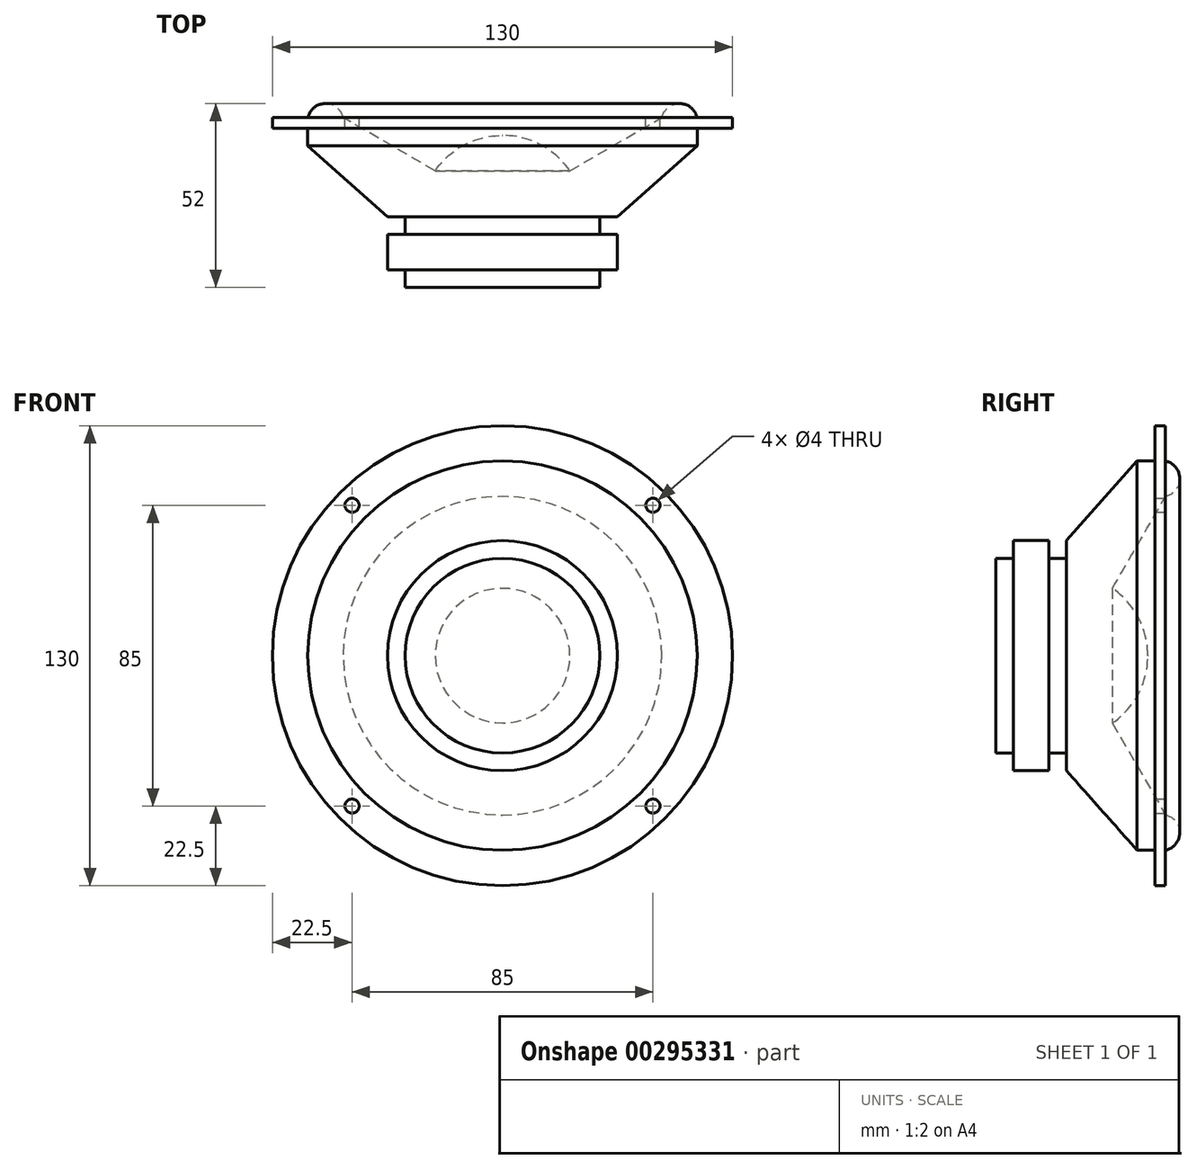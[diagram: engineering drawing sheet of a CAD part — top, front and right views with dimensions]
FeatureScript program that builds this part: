
annotation { "Feature Type Name" : "Feature", "Feature Type Description" : "" }
export const myFeature = defineFeature(function(context is Context, id is Id, definition is map)
    precondition{}
    {
        {
            var Q0;
            Q0=qCreatedBy(makeId("Front.planeOp"),FACE);
            var sketch = newSketch(context, id + "F0", { "sketchPlane" : qUnion([Q0])});
            skPoint(sketch, "E0.middle", {"position": v(0, 0) * mm});
            skCircle(sketch, "E1", {"center": v(0, 0) * mm, "radius": 55 * mm});
            skSolve(sketch);
        }
        {
            var Q0;
            Q0=makeQuery(id+"F0.imprint","IMPRINT",FACE,{"disambiguationData":[TD([[makeQuery(id+"F0.imprint","IMPRINT",EDGE,{"derivedFrom":sQuery(id+"F0.wireOp",EDGE,"E1")}),1.0]])]});
            extrude(context, id + "F1", {"entities" : qUnion([Q0]), "depth" : 25 * mm, "offsetDistance" : 25 * mm});
        }
        {
            var Q0;
            Q0=makeQuery(id+"F1.opExtrude","CAP_EDGE",EDGE,{"disambiguationData":[OSD([sQuery(id+"F0.wireOp",EDGE,"E1")])],"isStart":false});
            chamfer(context, id + "F2", {"entities" : qUnion([Q0]), "chamferType" : ChamferType.TWO_OFFSETS, "width1" : (45 / 2) * mm, "oppositeDirection" : false, "width2" : 20 * mm, "tangentPropagation" : true});
        }
        {
            var Q0;
            Q0=makeQuery(id+"F1.opExtrude","CAP_FACE",FACE,{"disambiguationData":[OSD([sQuery(id+"F0.wireOp",EDGE,"E1")])],"isStart":false});
            var sketch = newSketch(context, id + "F3", { "sketchPlane" : qUnion([Q0])});
            skCircle(sketch, "E2", {"center": v(0, 0) * mm, "radius": 27.5 * mm});
            skSolve(sketch);
        }
        {
            var Q0;
            Q0 = qSketchRegion(id + "F3", true);
            extrude(context, id + "F4", {"entities" : qUnion([Q0]), "depth" : 20 * mm, "offsetDistance" : 25 * mm});
        }
        {
            var Q0;
            Q0=makeQuery(id+"F4.opExtrude","CAP_FACE",FACE,{"disambiguationData":[OSD([sQuery(id+"F3.wireOp",EDGE,"E2")])],"isStart":false});
            var sketch = newSketch(context, id + "F5", { "sketchPlane" : qUnion([Q0])});
            skCircle(sketch, "E3", {"center": v(0, 0) * mm, "radius": 27.5 * mm});
            skCircle(sketch, "E4", {"center": v(0, 0) * mm, "radius": 32.5 * mm});
            skSolve(sketch);
        }
        {
            var Q0;
            Q0 = qSketchRegion(id + "F5", true);
            extrude(context, id + "F6", {"entities" : qUnion([Q0]), "operationType" : NewBodyOperationType.ADD, "endBound" : BoundingType.UP_TO_NEXT, "oppositeDirection" : true, "depth" : 10 * mm, "hasOffset" : true, "offsetDistance" : 5 * mm, "hasSecondDirection" : true, "secondDirectionOppositeDirection" : true, "secondDirectionDepth" : 5 * mm});
        }
        {
            var Q0;
            Q0=makeQuery(id+"F1.opExtrude","CAP_FACE",FACE,{"disambiguationData":[OSD([sQuery(id+"F0.wireOp",EDGE,"E1")])],"isStart":true});
            var sketch = newSketch(context, id + "F7", { "sketchPlane" : qUnion([Q0])});
            skCircle(sketch, "E5", {"center": v(0, 0) * mm, "radius": 65 * mm});
            skSolve(sketch);
        }
        {
            var Q0;
            Q0 = qSketchRegion(id + "F7", true);
            extrude(context, id + "F8", {"entities" : qUnion([Q0]), "operationType" : NewBodyOperationType.ADD, "depth" : 3 * mm, "offsetDistance" : 25 * mm});
        }
        {
            var Q0;
            Q0=makeQuery(id+"F8.opExtrude","CAP_FACE",FACE,{"disambiguationData":[OSD([sQuery(id+"F7.wireOp",EDGE,"E5")])],"isStart":false});
            var sketch = newSketch(context, id + "F9", { "sketchPlane" : qUnion([Q0])});
            skLineSegment(sketch, "E6.bottom", {"start": v(42.5, 42.5) * mm, "end": v(-42.5, 42.5) * mm, "construction": true});
            skLineSegment(sketch, "E6.top", {"start": v(42.5, -42.5) * mm, "end": v(-42.5, -42.5) * mm, "construction": true});
            skLineSegment(sketch, "E6.left", {"start": v(42.5, 42.5) * mm, "end": v(42.5, -42.5) * mm, "construction": true});
            skLineSegment(sketch, "E6.right", {"start": v(-42.5, 42.5) * mm, "end": v(-42.5, -42.5) * mm, "construction": true});
            skPoint(sketch, "E6.middle", {"position": v(0, 0) * mm});
            skCircle(sketch, "E7", {"center": v(-42.5, 42.5) * mm, "radius": 2 * mm});
            skCircle(sketch, "E8", {"center": v(42.5, 42.5) * mm, "radius": 2 * mm});
            skCircle(sketch, "E9", {"center": v(42.5, -42.5) * mm, "radius": 2 * mm});
            skCircle(sketch, "E10", {"center": v(-42.5, -42.5) * mm, "radius": 2 * mm});
            skSolve(sketch);
        }
        {
            var Q0;
            Q0 = qSketchRegion(id + "F9", true);
            extrude(context, id + "F10", {"entities" : qUnion([Q0]), "operationType" : NewBodyOperationType.REMOVE, "oppositeDirection" : true, "depth" : 25 * mm, "offsetDistance" : 25 * mm});
        }
        {
            var Q0;
            {var subQ0=sQuery(id+"F7.wireOp",EDGE,"E5");Q0=makeQuery(id+"FatyRIqTTuHNhlh_2.boolean.opBoolean","MERGE",FACE,{"derivedFrom":[makeQuery(id+"F8.opExtrude","CAP_FACE",FACE,{"disambiguationData":[OSD([subQ0])],"isStart":false}),makeQuery(id+"FatyRIqTTuHNhlh_2.opExtrude","CAP_FACE",FACE,{"disambiguationData":[OSD([subQ0,sQuery(id+"FaATDU1hy0XoADp_2.wireOp",EDGE,"dcB08ZIa-KRAl-nOKl-CVy3-LE7ijL8snLUQ")])],"isStart":true}),makeQuery(id+"FatyRIqTTuHNhlh_2.opExtrude","CAP_FACE",FACE,{"disambiguationData":[OSD([subQ0,sQuery(id+"FaATDU1hy0XoADp_2.wireOp",EDGE,"e9bd69b6-5c76-43c4-bfeb-50936e70dc3c.1.0")])],"isStart":true}),makeQuery(id+"FatyRIqTTuHNhlh_2.opExtrude","CAP_FACE",FACE,{"disambiguationData":[OSD([subQ0,sQuery(id+"FaATDU1hy0XoADp_2.wireOp",EDGE,"e9bd69b6-5c76-43c4-bfeb-50936e70dc3c.2.0")])],"isStart":true}),makeQuery(id+"FatyRIqTTuHNhlh_2.opExtrude","CAP_FACE",FACE,{"disambiguationData":[OSD([subQ0,sQuery(id+"FaATDU1hy0XoADp_2.wireOp",EDGE,"e9bd69b6-5c76-43c4-bfeb-50936e70dc3c.3.0")])],"isStart":true})]});}
            var sketch = newSketch(context, id + "F11", { "sketchPlane" : qUnion([Q0])});
            skCircle(sketch, "E11", {"center": v(0, 0) * mm, "radius": 45 * mm});
            skSolve(sketch);
        }
        {
            var Q0;
            Q0 = qSketchRegion(id + "F11", true);
            extrude(context, id + "F12", {"entities" : qUnion([Q0]), "operationType" : NewBodyOperationType.REMOVE, "oppositeDirection" : true, "depth" : 15 * mm, "offsetDistance" : 25 * mm, "hasDraft" : true, "draftAngle" : 60 * degree, "draftPullDirection" : true});
        }
        {
            var Q0;
            Q0=makeQuery(id+"F12.boolean.opBoolean","COPY",FACE,{"derivedFrom":makeQuery(id+"F12.opExtrude","CAP_FACE",FACE,{"disambiguationData":[OSD([sQuery(id+"F11.wireOp",EDGE,"E11")])],"isStart":false})});
            extrude(context, id + "F13", {"entities" : qUnion([Q0]), "operationType" : NewBodyOperationType.ADD, "depth" : 10 * mm, "offsetDistance" : 25 * mm});
        }
        {
            var Q0;
            Q0=makeQuery(id+"F13.opExtrude","CAP_EDGE",EDGE,{"disambiguationData":[OSD([sQuery(id+"F11.wireOp",EDGE,"E11")])],"isStart":false});
            fillet(context, id + "F14", {"entities" : qUnion([Q0]), "radius" : 23 * mm, "tangentPropagation" : true, "allowEdgeOverflow" : false});
        }
        {
            var Q0;
            {var subQ0=sQuery(id+"F7.wireOp",EDGE,"E5");Q0=makeQuery(id+"FatyRIqTTuHNhlh_2.boolean.opBoolean","MERGE",FACE,{"derivedFrom":[makeQuery(id+"F8.opExtrude","CAP_FACE",FACE,{"disambiguationData":[OSD([subQ0])],"isStart":false}),makeQuery(id+"FatyRIqTTuHNhlh_2.opExtrude","CAP_FACE",FACE,{"disambiguationData":[OSD([subQ0,sQuery(id+"FaATDU1hy0XoADp_2.wireOp",EDGE,"dcB08ZIa-KRAl-nOKl-CVy3-LE7ijL8snLUQ")])],"isStart":true}),makeQuery(id+"FatyRIqTTuHNhlh_2.opExtrude","CAP_FACE",FACE,{"disambiguationData":[OSD([subQ0,sQuery(id+"FaATDU1hy0XoADp_2.wireOp",EDGE,"e9bd69b6-5c76-43c4-bfeb-50936e70dc3c.1.0")])],"isStart":true}),makeQuery(id+"FatyRIqTTuHNhlh_2.opExtrude","CAP_FACE",FACE,{"disambiguationData":[OSD([subQ0,sQuery(id+"FaATDU1hy0XoADp_2.wireOp",EDGE,"e9bd69b6-5c76-43c4-bfeb-50936e70dc3c.2.0")])],"isStart":true}),makeQuery(id+"FatyRIqTTuHNhlh_2.opExtrude","CAP_FACE",FACE,{"disambiguationData":[OSD([subQ0,sQuery(id+"FaATDU1hy0XoADp_2.wireOp",EDGE,"e9bd69b6-5c76-43c4-bfeb-50936e70dc3c.3.0")])],"isStart":true})]});}
            var sketch = newSketch(context, id + "F15", { "sketchPlane" : qUnion([Q0])});
            skCircle(sketch, "E12", {"center": v(0, 0) * mm, "radius": 45 * mm});
            skCircle(sketch, "E13", {"center": v(0, 0) * mm, "radius": 55 * mm});
            skSolve(sketch);
        }
        {
            var Q0;
            Q0 = qSketchRegion(id + "F15", true);
            extrude(context, id + "F16", {"entities" : qUnion([Q0]), "operationType" : NewBodyOperationType.ADD, "depth" : 4 * mm, "offsetDistance" : 25 * mm});
        }
        {
            var Q0;
            Q0=makeQuery(id+"F16.opExtrude","CAP_EDGE",EDGE,{"disambiguationData":[OSD([sQuery(id+"F15.wireOp",EDGE,"E13")])],"isStart":false});
            var Q1;
            Q1=makeQuery(id+"F16.opExtrude","CAP_EDGE",EDGE,{"disambiguationData":[OSD([sQuery(id+"F15.wireOp",EDGE,"E12")])],"isStart":false});
            fillet(context, id + "F17", {"entities" : qUnion([Q0, Q1]), "radius" : 5.1 * mm, "tangentPropagation" : true, "allowEdgeOverflow" : false});
        }
    });
